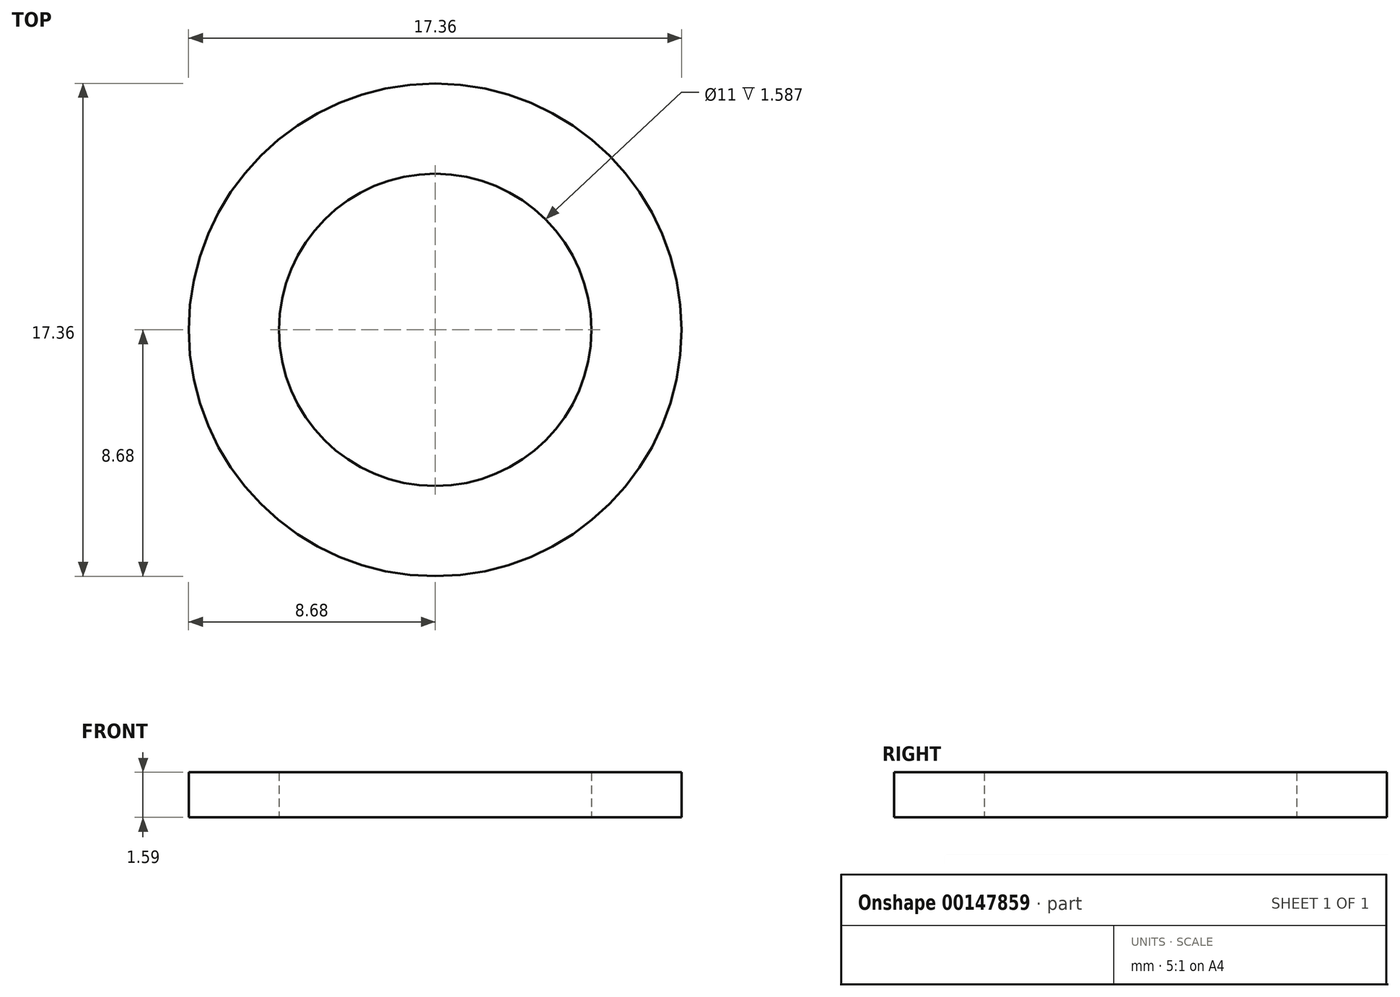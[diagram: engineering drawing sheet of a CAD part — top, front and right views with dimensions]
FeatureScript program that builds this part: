
annotation { "Feature Type Name" : "Feature", "Feature Type Description" : "" }
export const myFeature = defineFeature(function(context is Context, id is Id, definition is map)
    precondition{}
    {
        {
            var Q0;
            Q0=qCreatedBy(makeId("Top.planeOp"),FACE);
            var sketch = newSketch(context, id + "F0", { "sketchPlane" : qUnion([Q0])});
            skCircle(sketch, "E0", {"center": v(0, 0) * mm, "radius": 5.5 * mm});
            skCircle(sketch, "E1", {"center": v(0, 0) * mm, "radius": 8.68 * mm});
            skSolve(sketch);
        }
        {
            var Q0;
            Q0=qSketchRegion(id+"F0",true);
            extrude(context, id + "F1", {"entities" : qUnion([Q0]), "depth" : 1.59 * mm});
        }
    });
